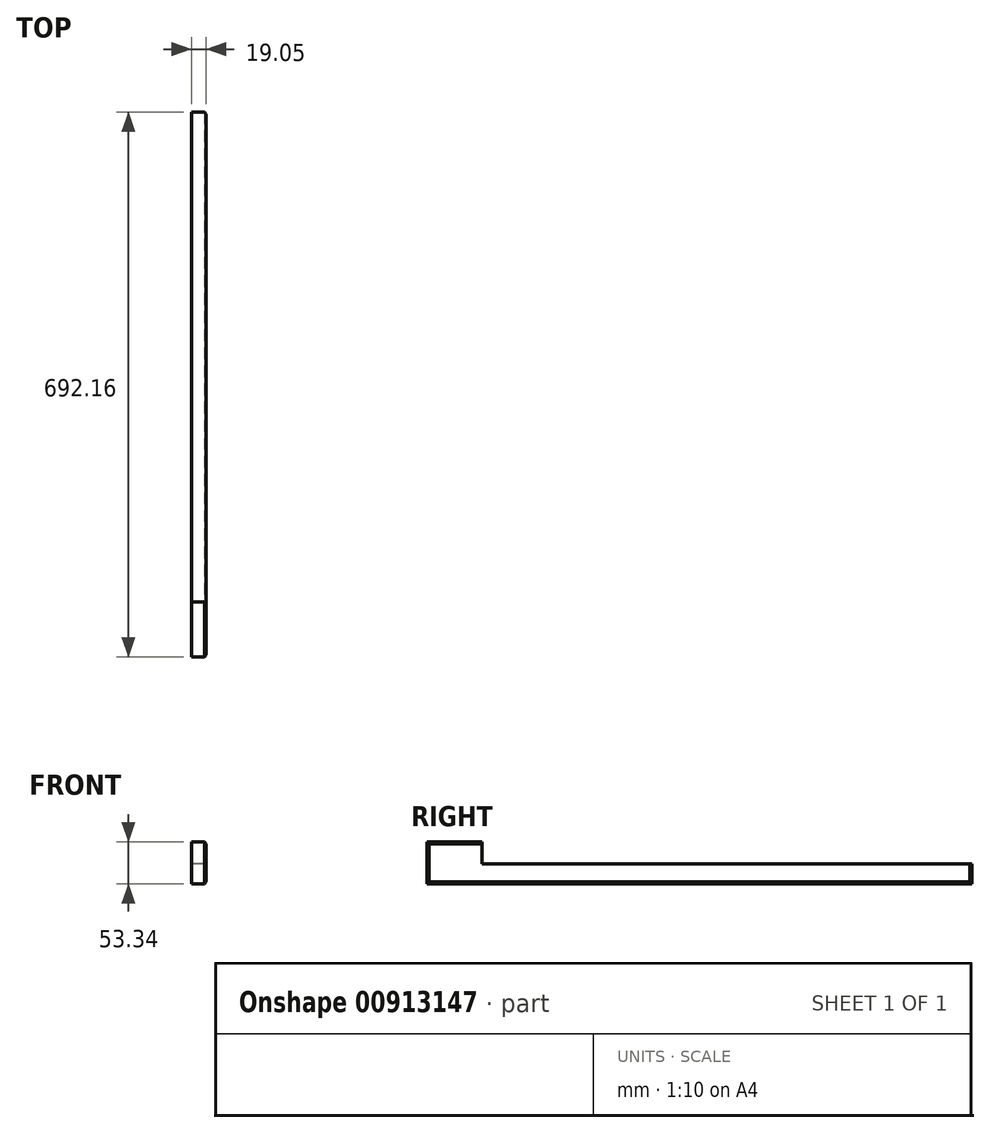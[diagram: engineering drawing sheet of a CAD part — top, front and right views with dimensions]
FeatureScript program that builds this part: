
annotation { "Feature Type Name" : "Feature", "Feature Type Description" : "" }
export const myFeature = defineFeature(function(context is Context, id is Id, definition is map)
    precondition{}
    {
        {
            var Q0;
            Q0=qCreatedBy(makeId("Right.planeOp"),FACE);
            var sketch = newSketch(context, id + "F0", { "sketchPlane" : qUnion([Q0])});
            skLineSegment(sketch, "E0.bottom", {"start": v(-346.08, -26.67) * mm, "end": v(346.08, -26.67) * mm});
            skLineSegment(sketch, "E0.top", {"start": v(-346.08, 26.67) * mm, "end": v(346.08, 26.67) * mm});
            skLineSegment(sketch, "E0.left", {"start": v(-346.08, -26.67) * mm, "end": v(-346.08, 26.67) * mm});
            skLineSegment(sketch, "E0.right", {"start": v(346.08, -26.67) * mm, "end": v(346.08, 26.67) * mm});
            skPoint(sketch, "E0.middle", {"position": v(0, 0) * mm});
            skLineSegment(sketch, "E1.bottom", {"start": v(346.08, 26.67) * mm, "end": v(-276.23, 26.67) * mm});
            skLineSegment(sketch, "E1.top", {"start": v(346.08, -1.27) * mm, "end": v(-276.23, -1.27) * mm});
            skLineSegment(sketch, "E1.left", {"start": v(346.08, 26.67) * mm, "end": v(346.08, -1.27) * mm});
            skLineSegment(sketch, "E1.right", {"start": v(-276.23, 26.67) * mm, "end": v(-276.23, -1.27) * mm});
            skSolve(sketch);
        }
        {
            var Q0;
            Q0=makeQuery(id+"F0.imprint","IMPRINT",FACE,{"disambiguationData":[TD([[makeQuery(id+"F0.imprint","IMPRINT",EDGE,{"derivedFrom":sQuery(id+"F0.wireOp",EDGE,"E0.bottom")}),1.0]])]});
            extrude(context, id + "F1", {"entities" : qUnion([Q0]), "depth" : 19.05 * mm, "offsetDistance" : 25.4 * mm});
        }
        {
            var Q0;
            Q0=makeQuery(id+"F1.opExtrude","CAP_EDGE",EDGE,{"disambiguationData":[OSD([sQuery(id+"F0.wireOp",EDGE,"E0.top")])],"isStart":false});
            var Q1;
            Q1=makeQuery(id+"F1.opExtrude","CAP_EDGE",EDGE,{"disambiguationData":[OSD([sQuery(id+"F0.wireOp",EDGE,"E0.left")])],"isStart":false});
            var Q2;
            Q2=makeQuery(id+"F1.opExtrude","CAP_EDGE",EDGE,{"disambiguationData":[OSD([sQuery(id+"F0.wireOp",EDGE,"E0.bottom")])],"isStart":false});
            var Q3;
            Q3=makeQuery(id+"F1.opExtrude","CAP_EDGE",EDGE,{"disambiguationData":[OSD([sQuery(id+"F0.wireOp",EDGE,"E0.right")])],"isStart":false});
            chamfer(context, id + "F2", {"entities" : qUnion([Q0, Q1, Q2, Q3]), "width" : 2.54 * mm, "tangentPropagation" : true});
        }
    });
